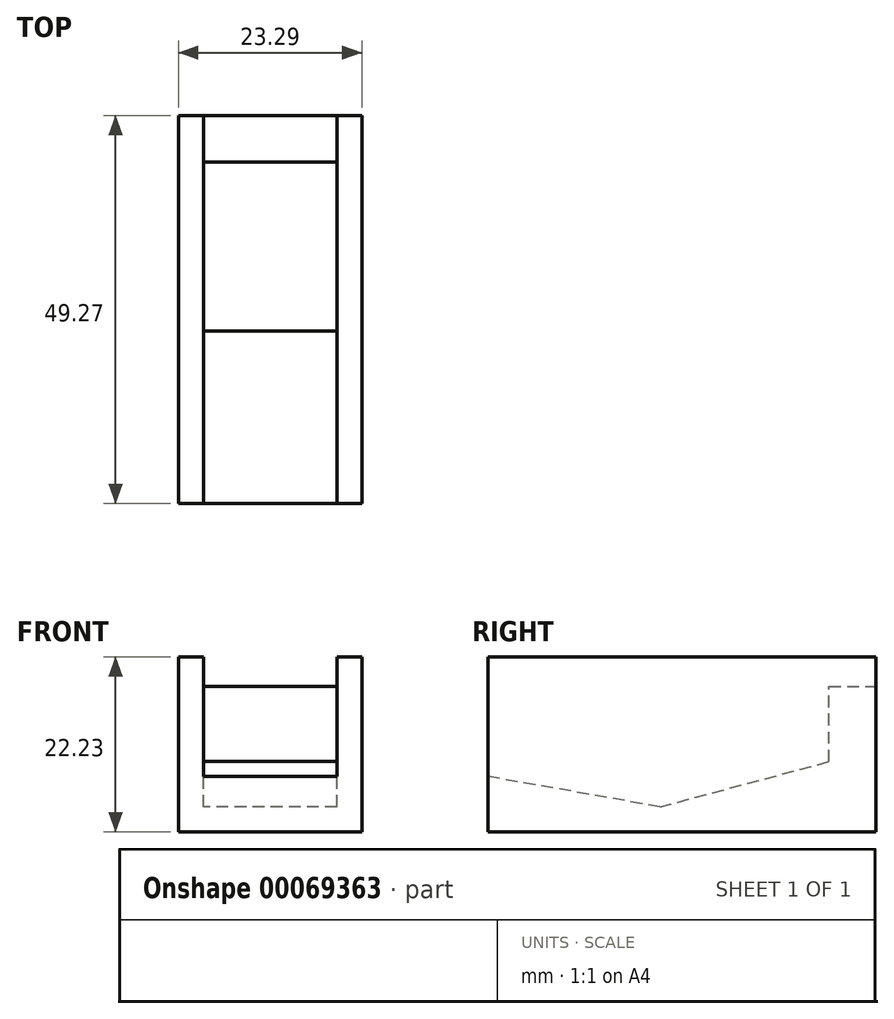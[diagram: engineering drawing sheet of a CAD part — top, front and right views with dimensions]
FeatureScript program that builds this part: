
annotation { "Feature Type Name" : "Feature", "Feature Type Description" : "" }
export const myFeature = defineFeature(function(context is Context, id is Id, definition is map)
    precondition{}
    {
        {
            var Q0;
            Q0=qCreatedBy(makeId("Right.planeOp"),FACE);
            var sketch = newSketch(context, id + "F0", { "sketchPlane" : qUnion([Q0])});
            skLineSegment(sketch, "E0", {"start": v(0, 0) * mm, "end": v(21.27, 0) * mm, "construction": true});
            skLineSegment(sketch, "E1", {"start": v(0, 0) * mm, "end": v(21.47, 5.75) * mm});
            skLineSegment(sketch, "E2", {"start": v(0, 0) * mm, "end": v(-21.89, 3.86) * mm});
            skLineSegment(sketch, "E3", {"start": v(21.47, 5.75) * mm, "end": v(21.47, 15.28) * mm});
            skLineSegment(sketch, "E4", {"start": v(21.47, 15.28) * mm, "end": v(27.38, 15.28) * mm});
            skLineSegment(sketch, "E5", {"start": v(27.38, 15.28) * mm, "end": v(27.38, -3.18) * mm});
            skLineSegment(sketch, "E6", {"start": v(-21.89, 3.86) * mm, "end": v(-21.89, -3.18) * mm});
            skLineSegment(sketch, "E7", {"start": v(-21.89, -3.18) * mm, "end": v(27.38, -3.18) * mm});
            skSolve(sketch);
        }
        {
            var Q0;
            Q0=makeQuery(id+"F0.imprint","IMPRINT",FACE,{"disambiguationData":[TD([[makeQuery(id+"F0.imprint","IMPRINT",EDGE,{"derivedFrom":sQuery(id+"F0.wireOp",EDGE,"E1")}),-1.0]])]});
            extrude(context, id + "F1", {"entities" : qUnion([Q0]), "depth" : 16.93 * mm});
        }
        {
            var Q0;
            Q0=qCreatedBy(makeId("Right.planeOp"),FACE);
            var sketch = newSketch(context, id + "F2", { "sketchPlane" : qUnion([Q0])});
            skLineSegment(sketch, "E8.bottom", {"start": v(-21.89, -3.18) * mm, "end": v(27.38, -3.18) * mm});
            skLineSegment(sketch, "E8.top", {"start": v(-21.89, 19.05) * mm, "end": v(27.38, 19.05) * mm});
            skLineSegment(sketch, "E8.left", {"start": v(-21.89, -3.18) * mm, "end": v(-21.89, 19.05) * mm});
            skLineSegment(sketch, "E8.right", {"start": v(27.38, -3.18) * mm, "end": v(27.38, 19.05) * mm});
            skPoint(sketch, "E9.0", {"position": v(27.38, -3.18) * mm});
            skPoint(sketch, "E10.0", {"position": v(-21.89, -3.18) * mm});
            skSolve(sketch);
        }
        {
            var Q0;
            Q0 = qSketchRegion(id + "F2", true);
            extrude(context, id + "F3", {"entities" : qUnion([Q0]), "operationType" : NewBodyOperationType.ADD, "oppositeDirection" : true, "depth" : 3.17 * mm});
        }
        {
            var Q0;
            Q0=makeQuery(id+"F1.opExtrude","CAP_FACE",FACE,{"disambiguationData":[OSD([sQuery(id+"F0.wireOp",EDGE,"E1"),sQuery(id+"F0.wireOp",EDGE,"E2"),sQuery(id+"F0.wireOp",EDGE,"E3"),sQuery(id+"F0.wireOp",EDGE,"E4"),sQuery(id+"F0.wireOp",EDGE,"E5"),sQuery(id+"F0.wireOp",EDGE,"E6"),sQuery(id+"F0.wireOp",EDGE,"E7")])],"isStart":false});
            var sketch = newSketch(context, id + "F4", { "sketchPlane" : qUnion([Q0])});
            skPoint(sketch, "E11.0", {"position": v(-21.89, -3.18) * mm});
            skPoint(sketch, "E12.0", {"position": v(27.38, 19.05) * mm});
            skLineSegment(sketch, "E13.bottom", {"start": v(-21.89, -3.18) * mm, "end": v(27.38, -3.18) * mm});
            skLineSegment(sketch, "E13.top", {"start": v(-21.89, 19.05) * mm, "end": v(27.38, 19.05) * mm});
            skLineSegment(sketch, "E13.left", {"start": v(-21.89, -3.18) * mm, "end": v(-21.89, 19.05) * mm});
            skLineSegment(sketch, "E13.right", {"start": v(27.38, -3.18) * mm, "end": v(27.38, 19.05) * mm});
            skSolve(sketch);
        }
        {
            var Q0;
            Q0 = qSketchRegion(id + "F4", true);
            extrude(context, id + "F5", {"entities" : qUnion([Q0]), "operationType" : NewBodyOperationType.ADD, "depth" : 3.17 * mm});
        }
    });
